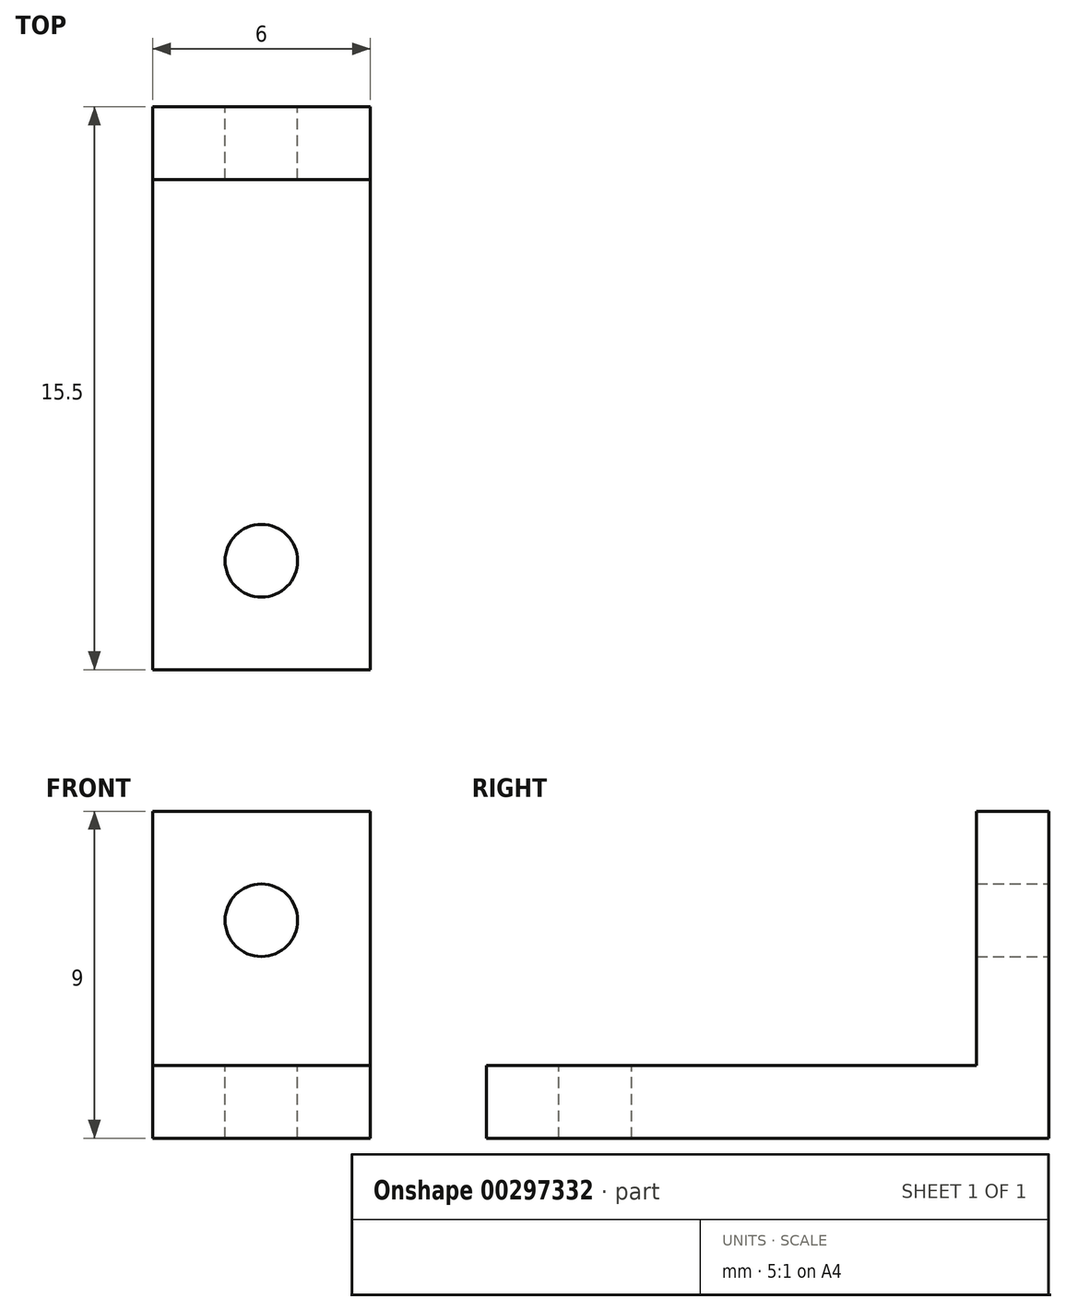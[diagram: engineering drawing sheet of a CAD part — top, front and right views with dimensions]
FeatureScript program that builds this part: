
annotation { "Feature Type Name" : "Feature", "Feature Type Description" : "" }
export const myFeature = defineFeature(function(context is Context, id is Id, definition is map)
    precondition{}
    {
        {
            var Q0;
            Q0=qCreatedBy(makeId("Front.planeOp"),FACE);
            var sketch = newSketch(context, id + "F0", { "sketchPlane" : qUnion([Q0])});
            skLineSegment(sketch, "E0.bottom", {"start": v(3, 4.5) * mm, "end": v(-3, 4.5) * mm});
            skLineSegment(sketch, "E0.top", {"start": v(3, -4.5) * mm, "end": v(-3, -4.5) * mm});
            skLineSegment(sketch, "E0.left", {"start": v(3, 4.5) * mm, "end": v(3, -4.5) * mm});
            skLineSegment(sketch, "E0.right", {"start": v(-3, 4.5) * mm, "end": v(-3, -4.5) * mm});
            skPoint(sketch, "E0.middle", {"position": v(0, 0) * mm});
            skCircle(sketch, "E1", {"center": v(0, 1.5) * mm, "radius": 1 * mm});
            skSolve(sketch);
        }
        {
            var Q0;
            Q0 = qSketchRegion(id + "F0", true);
            extrude(context, id + "F1", {"entities" : qUnion([Q0]), "depth" : 2 * mm});
        }
        {
            var Q0;
            Q0=makeQuery(id+"F1.opExtrude","CAP_FACE",FACE,{"disambiguationData":[OSD([sQuery(id+"F0.wireOp",EDGE,"E0.bottom"),sQuery(id+"F0.wireOp",EDGE,"E0.top"),sQuery(id+"F0.wireOp",EDGE,"E0.left"),sQuery(id+"F0.wireOp",EDGE,"E0.right"),sQuery(id+"F0.wireOp",EDGE,"E1")])],"isStart":false});
            var sketch = newSketch(context, id + "F2", { "sketchPlane" : qUnion([Q0])});
            skLineSegment(sketch, "E2.bottom", {"start": v(-3, -4.5) * mm, "end": v(3, -4.5) * mm});
            skLineSegment(sketch, "E2.top", {"start": v(-3, -2.5) * mm, "end": v(3, -2.5) * mm});
            skLineSegment(sketch, "E2.left", {"start": v(-3, -4.5) * mm, "end": v(-3, -2.5) * mm});
            skLineSegment(sketch, "E2.right", {"start": v(3, -4.5) * mm, "end": v(3, -2.5) * mm});
            skSolve(sketch);
        }
        {
            var Q0;
            Q0 = qSketchRegion(id + "F2", true);
            extrude(context, id + "F3", {"entities" : qUnion([Q0]), "operationType" : NewBodyOperationType.ADD, "depth" : 13.5 * mm});
        }
        {
            var Q0;
            Q0=makeQuery(id+"F3.opExtrude","SWEPT_FACE",FACE,{"disambiguationData":[OSD([sQuery(id+"F2.wireOp",EDGE,"E2.top")])]});
            var sketch = newSketch(context, id + "F4", { "sketchPlane" : qUnion([Q0])});
            skCircle(sketch, "E3", {"center": v(0, -12.5) * mm, "radius": 1 * mm});
            skSolve(sketch);
        }
        {
            var Q0;
            Q0 = qSketchRegion(id + "F4", true);
            extrude(context, id + "F5", {"entities" : qUnion([Q0]), "operationType" : NewBodyOperationType.REMOVE, "oppositeDirection" : true, "depth" : 25 * mm});
        }
    });
